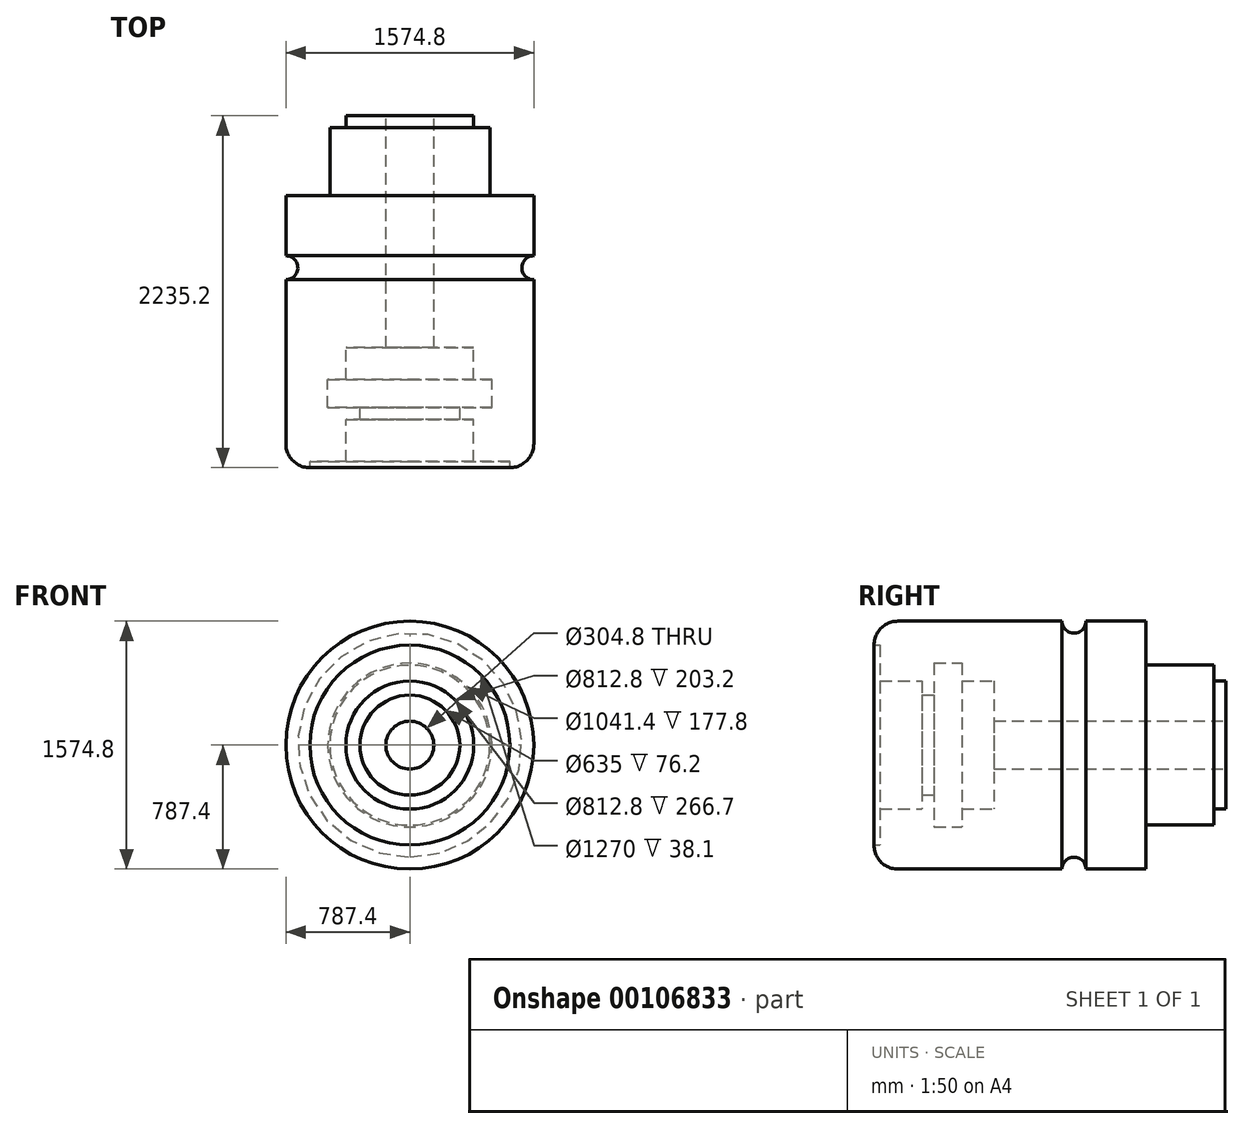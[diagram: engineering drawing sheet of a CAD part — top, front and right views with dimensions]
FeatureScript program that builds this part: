
annotation { "Feature Type Name" : "Feature", "Feature Type Description" : "" }
export const myFeature = defineFeature(function(context is Context, id is Id, definition is map)
    precondition{}
    {
        {
            var Q0;
            Q0=qCreatedBy(makeId("Right.planeOp"),FACE);
            var sketch = newSketch(context, id + "F0", { "sketchPlane" : qUnion([Q0])});
            skLineSegment(sketch, "E0", {"start": v(0, 0) * mm, "end": v(0, 635) * mm});
            skLineSegment(sketch, "E1", {"start": v(152.4, 787.4) * mm, "end": v(1727.2, 787.4) * mm});
            skLineSegment(sketch, "E2", {"start": v(1727.2, 787.4) * mm, "end": v(1727.2, 0) * mm});
            skLineSegment(sketch, "E3", {"start": v(1727.2, 508) * mm, "end": v(2159, 508) * mm});
            skLineSegment(sketch, "E4", {"start": v(2159, 508) * mm, "end": v(2159, 0) * mm});
            skLineSegment(sketch, "E5", {"start": v(2159, 406.4) * mm, "end": v(2235.2, 406.4) * mm});
            skLineSegment(sketch, "E6", {"start": v(2235.2, 406.4) * mm, "end": v(2235.2, 0) * mm});
            skLineSegment(sketch, "E7", {"start": v(0, 787.4) * mm, "end": v(1270, 787.4) * mm, "construction": true});
            skCircle(sketch, "E8", {"center": v(1270, 787.4) * mm, "radius": 76.2 * mm});
            skLineSegment(sketch, "E9", {"start": v(0, 0) * mm, "end": v(2235.2, 0) * mm});
            skPoint(sketch, "E10.visualSharp", {"position": v(0, 787.4) * mm});
            skArc(sketch, "E10.filletArc", {"start": v(152.4, 787.4) * mm, "mid": v(44.64, 742.76) * mm, "end": v(0, 635) * mm});
            skSolve(sketch);
        }
        {
            var Q0;
            {var subQ3=sQuery(id+"F0.wireOp",EDGE,"E5");Q0=makeQuery(id+"F0.imprint","IMPRINT",FACE,{"disambiguationData":[TD([[makeQuery(id+"F0.imprint","IMPRINT",EDGE,{"derivedFrom":subQ3}),-1.0]])]});}
            var Q1;
            {var subQ4=sQuery(id+"F0.wireOp",EDGE,"E3");Q1=makeQuery(id+"F0.imprint","IMPRINT",FACE,{"disambiguationData":[TD([[makeQuery(id+"F0.imprint","IMPRINT",EDGE,{"derivedFrom":subQ4}),-1.0]])]});}
            var Q2;
            {var subQ6=sQuery(id+"F0.wireOp",EDGE,"E0");Q2=makeQuery(id+"F0.imprint","IMPRINT",FACE,{"disambiguationData":[TD([[makeQuery(id+"F0.imprint","IMPRINT",EDGE,{"derivedFrom":subQ6}),-1.0]])]});}
            var Q3;
            Q3=sQuery(id+"F0.wireOp",EDGE,"E9");
            revolve(context, id + "F1", {"entities" : qUnion([Q0, Q1, Q2]), "axis" : qUnion([Q3]), "revolveType" : RevolveType.FULL});
        }
        {
            var Q0;
            Q0=qCreatedBy(makeId("Right.planeOp"),FACE);
            var sketch = newSketch(context, id + "F2", { "sketchPlane" : qUnion([Q0])});
            skLineSegment(sketch, "E11", {"start": v(0, 0) * mm, "end": v(2235.2, 0) * mm});
            skLineSegment(sketch, "E12", {"start": v(0, 0) * mm, "end": v(0, 635) * mm});
            skLineSegment(sketch, "E13", {"start": v(0, 635) * mm, "end": v(38.1, 635) * mm});
            skLineSegment(sketch, "E14", {"start": v(38.1, 635) * mm, "end": v(38.1, 406.4) * mm});
            skLineSegment(sketch, "E15", {"start": v(38.1, 406.4) * mm, "end": v(304.8, 406.4) * mm});
            skLineSegment(sketch, "E16", {"start": v(304.8, 406.4) * mm, "end": v(304.8, 317.5) * mm});
            skLineSegment(sketch, "E17", {"start": v(304.8, 317.5) * mm, "end": v(381, 317.5) * mm});
            skLineSegment(sketch, "E18", {"start": v(381, 317.5) * mm, "end": v(381, 520.7) * mm});
            skLineSegment(sketch, "E19", {"start": v(381, 520.7) * mm, "end": v(558.8, 520.7) * mm});
            skLineSegment(sketch, "E20", {"start": v(558.8, 520.7) * mm, "end": v(558.8, 406.4) * mm});
            skLineSegment(sketch, "E21", {"start": v(558.8, 406.4) * mm, "end": v(762, 406.4) * mm});
            skLineSegment(sketch, "E22", {"start": v(762, 406.4) * mm, "end": v(762, 152.4) * mm});
            skLineSegment(sketch, "E23", {"start": v(2235.2, 0) * mm, "end": v(2235.2, 152.4) * mm});
            skLineSegment(sketch, "E24", {"start": v(2235.2, 152.4) * mm, "end": v(762, 152.4) * mm});
            skSolve(sketch);
        }
        {
            var Q0;
            Q0 = qSketchRegion(id + "F2", true);
            var Q1;
            Q1=sQuery(id+"F2.wireOp",EDGE,"E11");
            revolve(context, id + "F3", {"operationType" : NewBodyOperationType.REMOVE, "entities" : qUnion([Q0]), "axis" : qUnion([Q1]), "revolveType" : RevolveType.FULL, "oppositeDirection" : true});
        }
    });
